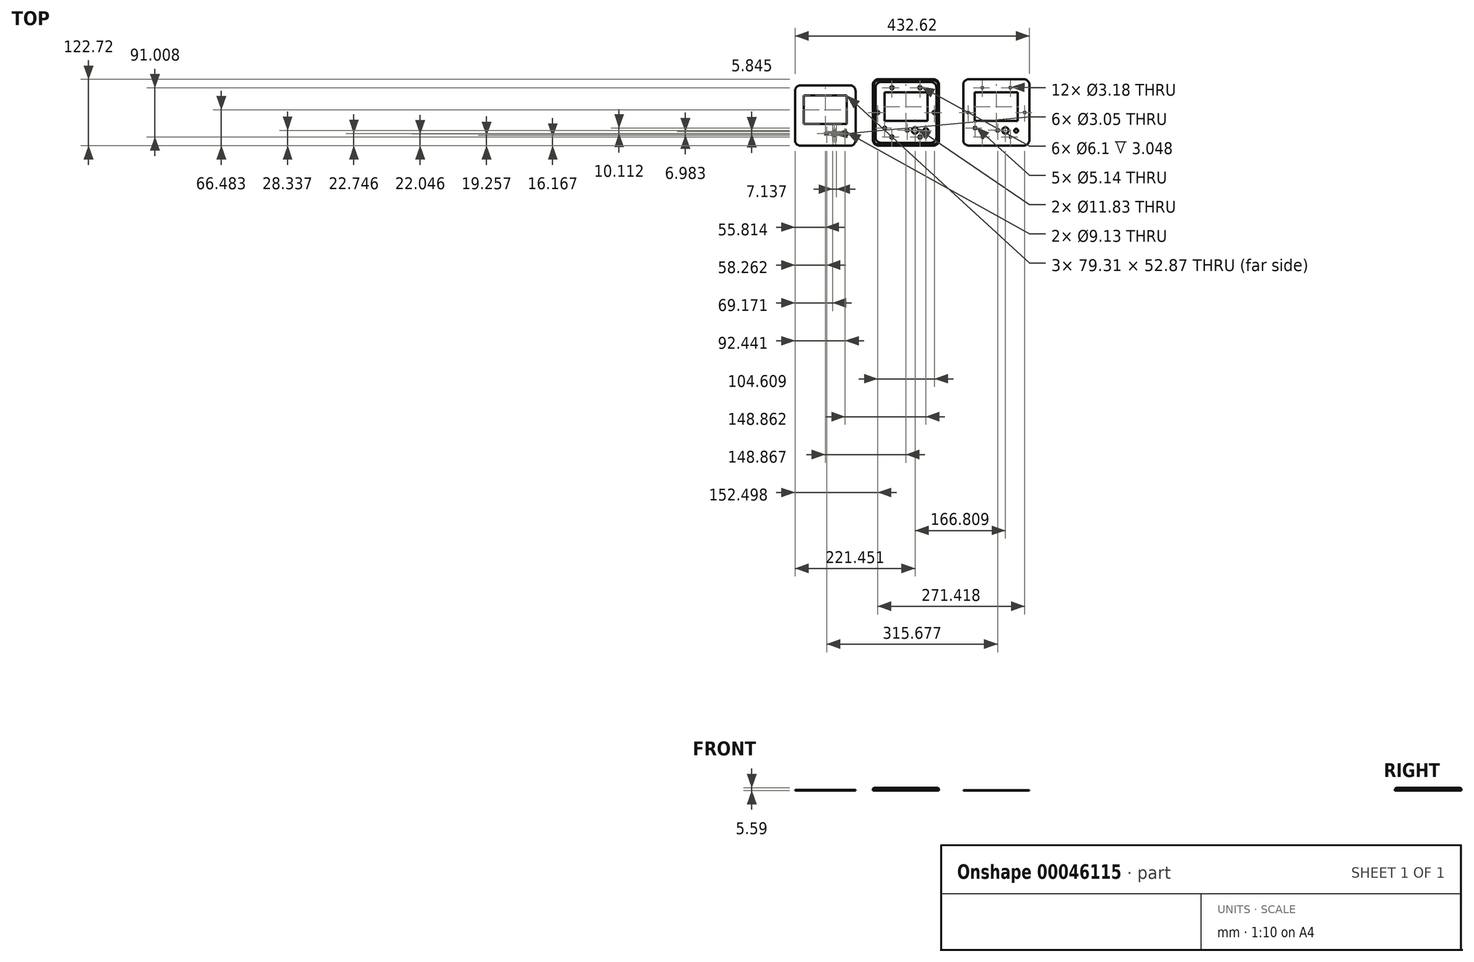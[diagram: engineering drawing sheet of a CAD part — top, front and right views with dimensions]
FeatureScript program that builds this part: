
annotation { "Feature Type Name" : "Feature", "Feature Type Description" : "" }
export const myFeature = defineFeature(function(context is Context, id is Id, definition is map)
    precondition{}
    {
        {
            var Q0;
            Q0=qCreatedBy(makeId("Top.planeOp"),FACE);
            var sketch = newSketch(context, id + "F0", { "sketchPlane" : qUnion([Q0])});
            skLineSegment(sketch, "E0", {"start": v(-62.44, 59.51) * mm, "end": v(-62.44, -62.74) * mm});
            skLineSegment(sketch, "E1", {"start": v(59.8, -62.74) * mm, "end": v(-62.44, -62.74) * mm});
            skLineSegment(sketch, "E2", {"start": v(59.8, 59.51) * mm, "end": v(59.8, -62.74) * mm});
            skLineSegment(sketch, "E3", {"start": v(-62.44, 59.51) * mm, "end": v(59.8, 59.51) * mm});
            skLineSegment(sketch, "E4", {"start": v(104.37, 59.51) * mm, "end": v(104.37, -62.74) * mm});
            skLineSegment(sketch, "E5", {"start": v(226.62, -62.74) * mm, "end": v(104.37, -62.74) * mm});
            skLineSegment(sketch, "E6", {"start": v(226.62, 59.51) * mm, "end": v(226.62, -62.74) * mm});
            skLineSegment(sketch, "E7", {"start": v(104.37, 59.51) * mm, "end": v(226.62, 59.51) * mm});
            skLineSegment(sketch, "E8", {"start": v(205.15, 35.55) * mm, "end": v(125.83, 35.55) * mm});
            skLineSegment(sketch, "E9", {"start": v(205.15, -17.32) * mm, "end": v(125.83, -17.32) * mm});
            skLineSegment(sketch, "E10", {"start": v(125.83, 35.55) * mm, "end": v(125.83, -17.32) * mm});
            skLineSegment(sketch, "E11", {"start": v(205.15, 35.55) * mm, "end": v(205.15, -17.32) * mm});
            skLineSegment(sketch, "E12", {"start": v(242.05, 59.51) * mm, "end": v(242.05, -1.85) * mm});
            skLineSegment(sketch, "E13", {"start": v(119.4, -80) * mm, "end": v(224.01, -80) * mm});
            skCircle(sketch, "E14", {"center": v(217.92, -1.85) * mm, "radius": 1.6 * mm});
            skCircle(sketch, "E15", {"center": v(113.3, -1.85) * mm, "radius": 1.6 * mm});
            skCircle(sketch, "E16", {"center": v(191.37, -47.04) * mm, "radius": 1.6 * mm});
            skCircle(sketch, "E17", {"center": v(139.61, -47.04) * mm, "radius": 1.6 * mm});
            skCircle(sketch, "E18", {"center": v(191.37, 43.97) * mm, "radius": 1.6 * mm});
            skCircle(sketch, "E19", {"center": v(139.61, 43.97) * mm, "radius": 1.6 * mm});
            skLineSegment(sketch, "E20", {"start": v(165.5, 43.97) * mm, "end": v(165.5, 35.55) * mm});
            skLineSegment(sketch, "E21", {"start": v(139.61, 43.97) * mm, "end": v(191.37, 43.97) * mm});
            skCircle(sketch, "E22", {"center": v(202.11, -35.32) * mm, "radius": 3.56 * mm});
            skCircle(sketch, "E23", {"center": v(182.26, -34.87) * mm, "radius": 5.91 * mm});
            skLineSegment(sketch, "E24", {"start": v(165.5, 43.97) * mm, "end": v(165.5, 59.51) * mm});
            skLineSegment(sketch, "E25", {"start": v(38.34, 35.55) * mm, "end": v(-40.97, 35.55) * mm});
            skLineSegment(sketch, "E26", {"start": v(38.34, -17.32) * mm, "end": v(-40.97, -17.32) * mm});
            skLineSegment(sketch, "E27", {"start": v(-40.97, 35.55) * mm, "end": v(-40.97, -17.32) * mm});
            skLineSegment(sketch, "E28", {"start": v(38.34, 35.55) * mm, "end": v(38.34, -17.32) * mm});
            skCircle(sketch, "E29", {"center": v(51.1, -1.85) * mm, "radius": 1.6 * mm});
            skCircle(sketch, "E30", {"center": v(-53.5, -1.85) * mm, "radius": 1.6 * mm});
            skCircle(sketch, "E31", {"center": v(24.56, -47.04) * mm, "radius": 1.6 * mm});
            skCircle(sketch, "E32", {"center": v(-27.2, -47.04) * mm, "radius": 1.6 * mm});
            skCircle(sketch, "E33", {"center": v(24.56, 43.97) * mm, "radius": 1.6 * mm});
            skCircle(sketch, "E34", {"center": v(-27.2, 43.97) * mm, "radius": 1.6 * mm});
            skLineSegment(sketch, "E35", {"start": v(-1.32, 43.97) * mm, "end": v(-1.32, 35.55) * mm});
            skLineSegment(sketch, "E36", {"start": v(-27.2, 43.97) * mm, "end": v(24.56, 43.97) * mm});
            skLineSegment(sketch, "E37", {"start": v(-1.32, 43.97) * mm, "end": v(-1.32, 59.51) * mm});
            skCircle(sketch, "E38", {"center": v(35.3, -35.32) * mm, "radius": 4.57 * mm});
            skCircle(sketch, "E39", {"center": v(126.26, -30.35) * mm, "radius": 2.57 * mm});
            skCircle(sketch, "E40", {"center": v(167.94, -34.62) * mm, "radius": 2.57 * mm});
            skCircle(sketch, "E41", {"center": v(-40.55, -30.35) * mm, "radius": 2.57 * mm});
            skCircle(sketch, "E42", {"center": v(1.13, -34.62) * mm, "radius": 2.57 * mm});
            skCircle(sketch, "E43", {"center": v(15.45, -34.87) * mm, "radius": 5.91 * mm});
            skSolve(sketch);
        }
        {
            var Q0;
            {var subQ1=sQuery(id+"F0.wireOp",EDGE,"E0");Q0=makeQuery(id+"F0.imprint","IMPRINT",FACE,{"disambiguationData":[TD([[makeQuery(id+"F0.imprint","IMPRINT",EDGE,{"derivedFrom":subQ1}),1.0]])]});}
            extrude(context, id + "F1", {"entities" : qUnion([Q0]), "depth" : 5.6 * mm, "offsetDistance" : 25.4 * mm});
        }
        {
            var Q0;
            Q0=makeQuery(id+"F1.opExtrude","SWEPT_EDGE",EDGE,{"disambiguationData":[OSD([sQuery(id+"F0.wireOp",EDGE,"E0"),sQuery(id+"F0.wireOp",EDGE,"E3")])]});
            var Q1;
            Q1=makeQuery(id+"F1.opExtrude","SWEPT_EDGE",EDGE,{"disambiguationData":[OSD([sQuery(id+"F0.wireOp",EDGE,"E0"),sQuery(id+"F0.wireOp",EDGE,"E1")])]});
            var Q2;
            Q2=makeQuery(id+"F1.opExtrude","SWEPT_EDGE",EDGE,{"disambiguationData":[OSD([sQuery(id+"F0.wireOp",EDGE,"E1"),sQuery(id+"F0.wireOp",EDGE,"E2")])]});
            var Q3;
            Q3=makeQuery(id+"F1.opExtrude","SWEPT_EDGE",EDGE,{"disambiguationData":[OSD([sQuery(id+"F0.wireOp",EDGE,"E2"),sQuery(id+"F0.wireOp",EDGE,"E3")])]});
            fillet(context, id + "F2", {"entities" : qUnion([Q0, Q1, Q2, Q3]), "radius" : 10.16 * mm, "tangentPropagation" : true, "allowEdgeOverflow" : false});
        }
        {
            var Q0;
            Q0=makeQuery(id+"F1.opExtrude","CAP_EDGE",EDGE,{"disambiguationData":[OSD([sQuery(id+"F0.wireOp",EDGE,"E3")])],"isStart":false});
            chamfer(context, id + "F3", {"entities" : qUnion([Q0]), "width" : 2.03 * mm, "tangentPropagation" : true});
        }
        {
            var Q0;
            {var subQ1=sQuery(id+"F0.wireOp",EDGE,"E4");Q0=makeQuery(id+"F0.imprint","IMPRINT",FACE,{"disambiguationData":[TD([[makeQuery(id+"F0.imprint","IMPRINT",EDGE,{"derivedFrom":subQ1}),1.0]])]});}
            extrude(context, id + "F4", {"entities" : qUnion([Q0]), "depth" : 0.64 * mm, "offsetDistance" : 25.4 * mm});
        }
        {
            var Q0;
            Q0=makeQuery(id+"F4.opExtrude","SWEPT_EDGE",EDGE,{"disambiguationData":[OSD([sQuery(id+"F0.wireOp",EDGE,"E4"),sQuery(id+"F0.wireOp",EDGE,"E5")])]});
            var Q1;
            Q1=makeQuery(id+"F4.opExtrude","SWEPT_EDGE",EDGE,{"disambiguationData":[OSD([sQuery(id+"F0.wireOp",EDGE,"E5"),sQuery(id+"F0.wireOp",EDGE,"E6")])]});
            var Q2;
            Q2=makeQuery(id+"F4.opExtrude","SWEPT_EDGE",EDGE,{"disambiguationData":[OSD([sQuery(id+"F0.wireOp",EDGE,"E4"),sQuery(id+"F0.wireOp",EDGE,"E7")])]});
            var Q3;
            Q3=makeQuery(id+"F4.opExtrude","SWEPT_EDGE",EDGE,{"disambiguationData":[OSD([sQuery(id+"F0.wireOp",EDGE,"E6"),sQuery(id+"F0.wireOp",EDGE,"E7")])]});
            fillet(context, id + "F5", {"entities" : qUnion([Q0, Q1, Q2, Q3]), "radius" : 10.16 * mm, "tangentPropagation" : true, "allowEdgeOverflow" : false});
        }
        {
            var Q0;
            Q0=makeQuery(id+"F1.opExtrude","CAP_FACE",FACE,{"disambiguationData":[OSD([sQuery(id+"F0.wireOp",EDGE,"E0"),sQuery(id+"F0.wireOp",EDGE,"E1"),sQuery(id+"F0.wireOp",EDGE,"E2"),sQuery(id+"F0.wireOp",EDGE,"E3"),sQuery(id+"F0.wireOp",EDGE,"E25"),sQuery(id+"F0.wireOp",EDGE,"E26"),sQuery(id+"F0.wireOp",EDGE,"E27"),sQuery(id+"F0.wireOp",EDGE,"E28"),sQuery(id+"F0.wireOp",EDGE,"E29"),sQuery(id+"F0.wireOp",EDGE,"E30"),sQuery(id+"F0.wireOp",EDGE,"E31"),sQuery(id+"F0.wireOp",EDGE,"E32"),sQuery(id+"F0.wireOp",EDGE,"E33"),sQuery(id+"F0.wireOp",EDGE,"E34"),sQuery(id+"F0.wireOp",EDGE,"79eb2f10-6eb3-4b36-ba18-e5e093a07e76"),sQuery(id+"F0.wireOp",EDGE,"de8b0483-b0b0-43f7-bfef-031b314bb3b6")])],"isStart":false});
            var sketch = newSketch(context, id + "F6", { "sketchPlane" : qUnion([Q0])});
            skLineSegment(sketch, "E44", {"start": v(-62.52, 0) * mm, "end": v(-57.51, 0) * mm});
            skLineSegment(sketch, "E45", {"start": v(54.82, 0) * mm, "end": v(59.83, 0) * mm});
            skLineSegment(sketch, "E46", {"start": v(-1.33, 59.52) * mm, "end": v(-1.33, 54.5) * mm});
            skLineSegment(sketch, "E47", {"start": v(-5, -62.74) * mm, "end": v(-5, -57.73) * mm});
            skLineSegment(sketch, "E48", {"start": v(-47.35, -57.73) * mm, "end": v(44.66, -57.73) * mm});
            skLineSegment(sketch, "E49", {"start": v(54.82, -47.57) * mm, "end": v(54.82, 44.35) * mm});
            skLineSegment(sketch, "E50", {"start": v(44.66, 54.5) * mm, "end": v(-47.35, 54.5) * mm});
            skLineSegment(sketch, "E51", {"start": v(-57.51, 44.35) * mm, "end": v(-57.51, -47.57) * mm});
            skPoint(sketch, "E52.visualSharp", {"position": v(-57.51, 54.5) * mm});
            skArc(sketch, "E52.filletArc", {"start": v(-47.35, 54.5) * mm, "mid": v(-54.54, 51.53) * mm, "end": v(-57.51, 44.35) * mm});
            skPoint(sketch, "E53.visualSharp", {"position": v(54.82, 54.5) * mm});
            skArc(sketch, "E53.filletArc", {"start": v(54.82, 44.35) * mm, "mid": v(51.84, 51.53) * mm, "end": v(44.66, 54.5) * mm});
            skPoint(sketch, "E54.visualSharp", {"position": v(54.82, -57.73) * mm});
            skArc(sketch, "E54.filletArc", {"start": v(44.66, -57.73) * mm, "mid": v(51.84, -54.75) * mm, "end": v(54.82, -47.57) * mm});
            skPoint(sketch, "E55.visualSharp", {"position": v(-57.51, -57.73) * mm});
            skArc(sketch, "E55.filletArc", {"start": v(-57.51, -47.57) * mm, "mid": v(-54.54, -54.75) * mm, "end": v(-47.35, -57.73) * mm});
            skSolve(sketch);
        }
        {
            var Q0;
            Q0 = qSketchRegion(id + "F6", true);
            extrude(context, id + "F7", {"entities" : qUnion([Q0]), "operationType" : NewBodyOperationType.REMOVE, "oppositeDirection" : true, "depth" : 1.27 * mm, "offsetDistance" : 25.4 * mm});
        }
        {
            var Q0;
            Q0=makeQuery(id+"F7.boolean.opBoolean","COPY",FACE,{"derivedFrom":makeQuery(id+"F7.opExtrude","CAP_FACE",FACE,{"disambiguationData":[OSD([sQuery(id+"F6.wireOp",EDGE,"E48"),sQuery(id+"F6.wireOp",EDGE,"E49"),sQuery(id+"F6.wireOp",EDGE,"E50"),sQuery(id+"F6.wireOp",EDGE,"E51"),sQuery(id+"F6.wireOp",EDGE,"E52.filletArc"),sQuery(id+"F6.wireOp",EDGE,"E53.filletArc"),sQuery(id+"F6.wireOp",EDGE,"E54.filletArc"),sQuery(id+"F6.wireOp",EDGE,"E55.filletArc")])],"isStart":false})});
            var sketch = newSketch(context, id + "F8", { "sketchPlane" : qUnion([Q0])});
            skCircle(sketch, "E56", {"center": v(-27.2, 43.97) * mm, "radius": 3.05 * mm});
            skCircle(sketch, "E57", {"center": v(24.56, 43.97) * mm, "radius": 3.05 * mm});
            skCircle(sketch, "E58", {"center": v(-27.2, -47.04) * mm, "radius": 3.05 * mm});
            skCircle(sketch, "E59", {"center": v(24.56, -47.04) * mm, "radius": 3.05 * mm});
            skCircle(sketch, "E60", {"center": v(-53.5, -1.85) * mm, "radius": 3.05 * mm});
            skCircle(sketch, "E61", {"center": v(51.1, -1.85) * mm, "radius": 3.05 * mm});
            skSolve(sketch);
        }
        {
            var Q0;
            Q0 = qSketchRegion(id + "F8", true);
            extrude(context, id + "F9", {"entities" : qUnion([Q0]), "operationType" : NewBodyOperationType.REMOVE, "oppositeDirection" : true, "depth" : 3.05 * mm, "offsetDistance" : 25.4 * mm});
        }
        {
            var Q0;
            Q0=qCreatedBy(makeId("Top.planeOp"),FACE);
            var sketch = newSketch(context, id + "F10", { "sketchPlane" : qUnion([Q0])});
            skLineSegment(sketch, "E62", {"start": v(-189.84, 29.7) * mm, "end": v(-110.53, 29.7) * mm});
            skLineSegment(sketch, "E63", {"start": v(-110.53, 29.7) * mm, "end": v(-110.53, -23.16) * mm});
            skLineSegment(sketch, "E64", {"start": v(-110.53, -23.16) * mm, "end": v(-189.84, -23.16) * mm});
            skLineSegment(sketch, "E65", {"start": v(-189.84, -23.16) * mm, "end": v(-189.84, 29.7) * mm});
            skCircle(sketch, "E66", {"center": v(-136.83, -38.95) * mm, "radius": 1.52 * mm});
            skCircle(sketch, "E67", {"center": v(-133.42, -40.72) * mm, "radius": 1.52 * mm});
            skCircle(sketch, "E68", {"center": v(-135.8, -43.66) * mm, "radius": 1.52 * mm});
            skCircle(sketch, "E69", {"center": v(-133.3, -36.97) * mm, "radius": 1.52 * mm});
            skCircle(sketch, "E70", {"center": v(-129.7, -39.49) * mm, "radius": 1.52 * mm});
            skCircle(sketch, "E71", {"center": v(-131.02, -43.95) * mm, "radius": 1.52 * mm});
            skCircle(sketch, "E72", {"center": v(-113.56, -41.16) * mm, "radius": 4.57 * mm});
            skCircle(sketch, "E73", {"center": v(-147.74, -40.46) * mm, "radius": 2.57 * mm});
            skLineSegment(sketch, "E74", {"start": v(-150.19, 29.7) * mm, "end": v(-150.19, 48.66) * mm});
            skLineSegment(sketch, "E75", {"start": v(-104.53, 48.3) * mm, "end": v(-195.84, 48.3) * mm});
            skLineSegment(sketch, "E76", {"start": v(-206, 38.14) * mm, "end": v(-206, -53.05) * mm});
            skArc(sketch, "E77.filletArc", {"start": v(-195.84, 48.3) * mm, "mid": v(-203.03, 45.32) * mm, "end": v(-206, 38.14) * mm});
            skArc(sketch, "E78.filletArc", {"start": v(-94.37, 38.14) * mm, "mid": v(-97.35, 45.32) * mm, "end": v(-104.53, 48.3) * mm});
            skArc(sketch, "E79.filletArc", {"start": v(-104.53, -63.2) * mm, "mid": v(-97.35, -60.23) * mm, "end": v(-94.37, -53.05) * mm});
            skArc(sketch, "E80.filletArc", {"start": v(-206, -53.05) * mm, "mid": v(-203.03, -60.23) * mm, "end": v(-195.84, -63.2) * mm});
            skLineSegment(sketch, "E81", {"start": v(-94.37, 38.14) * mm, "end": v(-94.37, -53.05) * mm});
            skLineSegment(sketch, "E82", {"start": v(-195.84, -63.2) * mm, "end": v(-104.53, -63.2) * mm});
            skSolve(sketch);
        }
        {
            var Q0;
            Q0 = qSketchRegion(id + "F10", true);
            extrude(context, id + "F11", {"entities" : qUnion([Q0]), "depth" : 1.27 * mm, "offsetDistance" : 25.4 * mm});
        }
    });
